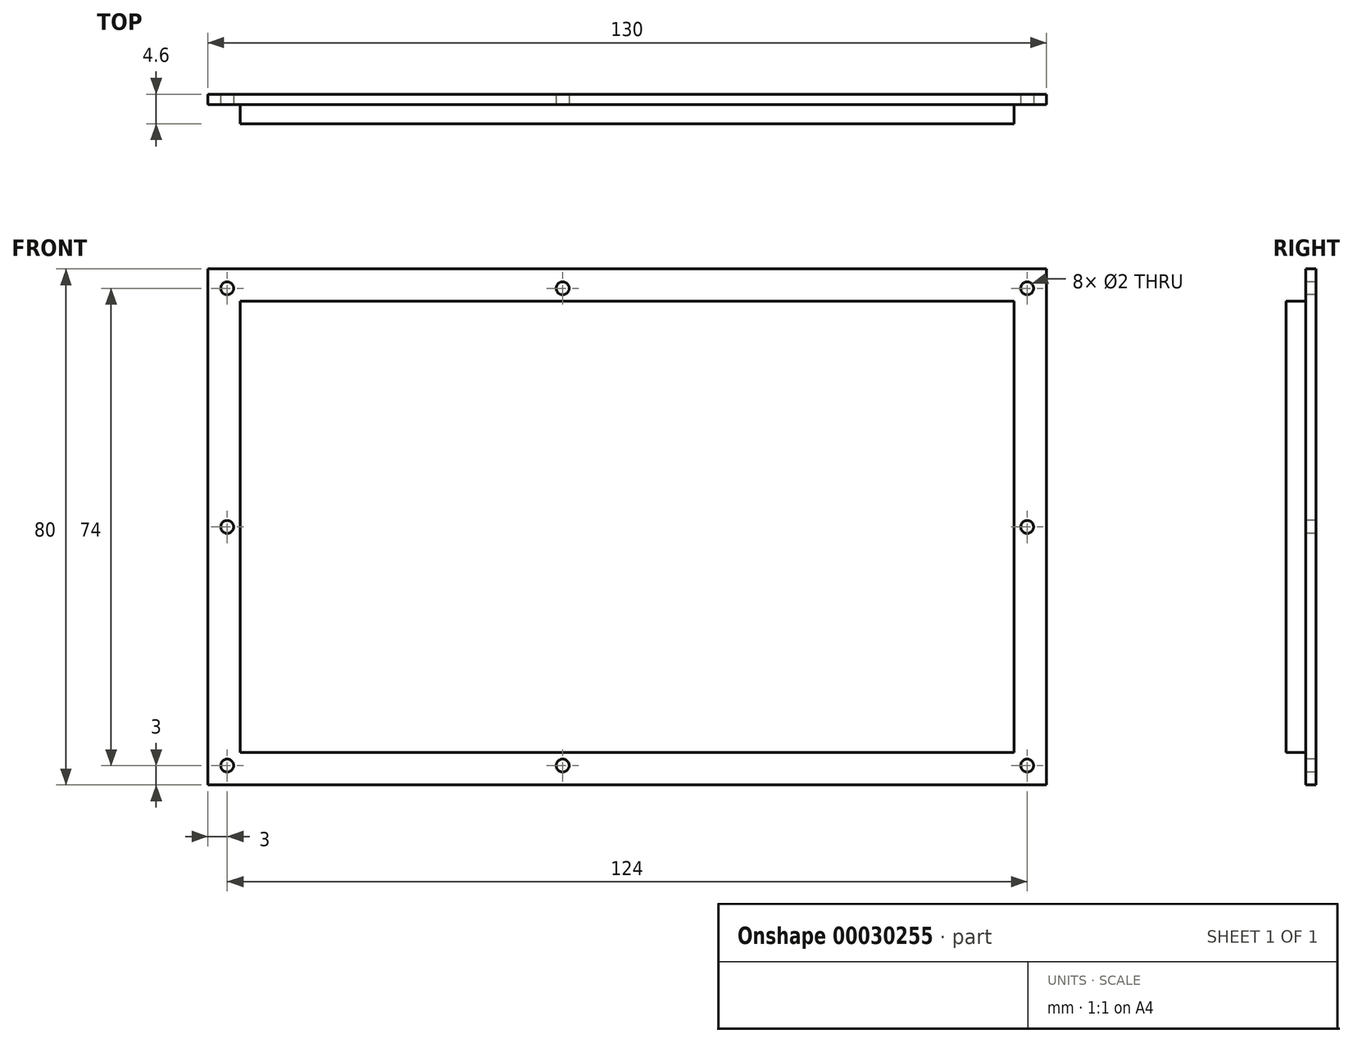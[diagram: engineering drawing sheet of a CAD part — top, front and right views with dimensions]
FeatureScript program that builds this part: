
annotation { "Feature Type Name" : "Feature", "Feature Type Description" : "" }
export const myFeature = defineFeature(function(context is Context, id is Id, definition is map)
    precondition{}
    {
        {
            var Q0;
            Q0=qCreatedBy(makeId("Front.planeOp"),FACE);
            var sketch = newSketch(context, id + "F0", { "sketchPlane" : qUnion([Q0])});
            skLineSegment(sketch, "E0.rect.bottom", {"start": v(60, -35) * mm, "end": v(-60, -35) * mm});
            skLineSegment(sketch, "E0.rect.top", {"start": v(60, 35) * mm, "end": v(-60, 35) * mm});
            skLineSegment(sketch, "E0.rect.left", {"start": v(60, -35) * mm, "end": v(60, 35) * mm});
            skLineSegment(sketch, "E0.rect.right", {"start": v(-60, -35) * mm, "end": v(-60, 35) * mm});
            skPoint(sketch, "E0.rect.middle", {"position": v(0, 0) * mm});
            skSolve(sketch);
        }
        {
            var Q0;
            Q0=qCreatedBy(makeId("Front.planeOp"),FACE);
            var sketch = newSketch(context, id + "F1", { "sketchPlane" : qUnion([Q0])});
            skLineSegment(sketch, "E1.bottom", {"start": v(65, 40) * mm, "end": v(-65, 40) * mm});
            skLineSegment(sketch, "E1.top", {"start": v(65, -40) * mm, "end": v(-65, -40) * mm});
            skLineSegment(sketch, "E1.left", {"start": v(65, 40) * mm, "end": v(65, -40) * mm});
            skLineSegment(sketch, "E1.right", {"start": v(-65, 40) * mm, "end": v(-65, -40) * mm});
            skPoint(sketch, "E2", {"position": v(62, 37) * mm});
            skPoint(sketch, "E3.MirrorP", {"position": v(62, -37) * mm});
            skPoint(sketch, "E4.MirrorP", {"position": v(-62, 37) * mm});
            skPoint(sketch, "E5.MirrorP", {"position": v(-62, -37) * mm});
            skPoint(sketch, "E6", {"position": v(-62, 0) * mm});
            skPoint(sketch, "E7.MirrorP", {"position": v(62, 0) * mm});
            skPoint(sketch, "E8", {"position": v(-10, -37) * mm});
            skPoint(sketch, "E9.MirrorP", {"position": v(-10, 37) * mm});
            skSolve(sketch);
        }
        {
            var Q0;
            Q0=makeQuery(id+"F0.imprint","IMPRINT",FACE,{"disambiguationData":[TD([[makeQuery(id+"F0.imprint","IMPRINT",EDGE,{"derivedFrom":sQuery(id+"F0.wireOp",EDGE,"E0.rect.bottom")}),-1.0]])]});
            extrude(context, id + "F2", {"entities" : qUnion([Q0]), "depth" : 3 * mm});
        }
        {
            var Q0;
            Q0=makeQuery(id+"F1.imprint","IMPRINT",FACE,{"disambiguationData":[TD([[makeQuery(id+"F1.imprint","IMPRINT",EDGE,{"derivedFrom":sQuery(id+"F1.wireOp",EDGE,"E1.bottom")}),1.0]])]});
            extrude(context, id + "F3", {"entities" : qUnion([Q0]), "operationType" : NewBodyOperationType.ADD, "oppositeDirection" : true, "depth" : 1.6 * mm});
        }
        {
            var Q0;
            Q0=sQuery(id+"F1.wireOp",VERTEX,"E2");
            var Q1;
            Q1=sQuery(id+"F1.wireOp",VERTEX,"E7.MirrorP");
            var Q2;
            Q2=sQuery(id+"F1.wireOp",VERTEX,"E3.MirrorP");
            var Q3;
            Q3=sQuery(id+"F1.wireOp",VERTEX,"ff2dbea7-a43b-457f-9169-24450f97a144");
            var Q4;
            Q4=sQuery(id+"F1.wireOp",VERTEX,"5de818be-ebce-4ef3-a94b-517ed82807950.MirrorP");
            var Q5;
            Q5=sQuery(id+"F1.wireOp",VERTEX,"E4.MirrorP");
            var Q6;
            Q6=sQuery(id+"F1.wireOp",VERTEX,"E6");
            var Q7;
            Q7=sQuery(id+"F1.wireOp",VERTEX,"E5.MirrorP");
            var Q8;
            Q8=sQuery(id+"F1.wireOp",VERTEX,"E9.MirrorP");
            var Q9;
            Q9=sQuery(id+"F1.wireOp",VERTEX,"E8");
            var Q10;
            Q10=makeQuery(id+"F2.opExtrude","SWEPT_BODY",BODY,{"disambiguationData":[OSD([sQuery(id+"F0.wireOp",EDGE,"E0.rect.bottom"),sQuery(id+"F0.wireOp",EDGE,"E0.rect.top"),sQuery(id+"F0.wireOp",EDGE,"E0.rect.left"),sQuery(id+"F0.wireOp",EDGE,"E0.rect.right")])]});
            hole(context, id + "F4", {"style" : HoleStyle.SIMPLE, "endStyle" : HoleEndStyle.THROUGH, "holeDiameter" : 2 * mm, "locations" : qUnion([Q0, Q1, Q2, Q3, Q4, Q5, Q6, Q7, Q8, Q9]), "scope" : qUnion([Q10]), "tappedDepth" : 12 * mm, "tapClearance" : 3});
        }
    });
